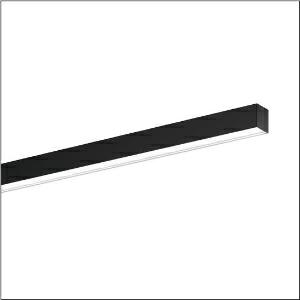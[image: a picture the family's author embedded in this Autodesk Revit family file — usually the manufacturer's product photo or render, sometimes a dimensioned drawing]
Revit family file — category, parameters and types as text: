
# Revit family: silica_r__21_51mx20tat2b_5805
name_source: partatom
category: Lighting Fixtures
units: mm (PartAtom-declared; Revit-internal decimal feet)

## family parameters
Cut with Voids When Loaded = No
Host = Face
Light Source = No
Part Type = Normal
Room Calculation Point = No
Round Connector Dimension = Use Diameter
Shared = No

## types (1)
- --- (1 x LED, 2400 lm, 20.5 W, 6500K)
    Apparent Load = 21 VA
    CIE Flux Codes = 48 79 96 100 100
    Color Rendering = 80
    Color Temperature = 6500K
    Default Elevation = 1800 mm
    Description = Silica® 21, office luminaire, primary optical cover: cover, of PMMA, opal, light emission: direct distribution, primary light characteristic: symmetric, installation type: surface-mounted, LED, rated luminous flux: 2.400lm, luminous efficacy: 112lm/W, light colour: 8tw, colour temperature: 2700..6500K, control gear: ECG DALI, with terminal, 3+2-pole, max. 2.5mm², mains connection: 220..240V, AC, 50/60Hz, rated input power: 21.5W, luminaire housing, of aluminium, jet black (RAL 9005), length: 1.204mm, width: 53mm, height: 53mm, protection rating (complete): IP20, insulation class (complete): insulation class I (protective earthing), certification: CE, permissible operating ambient temperature: 0..+35°C, standard: EN 50419, packaging unit: 1 piece
    Height = 0 mm  [stored 0 ft]
    Lamp = 1 x LED
    Lamp Light Flux = 2400 lm
    Lamp Power = 20.5 W
    Lamp count = 1
    Length = 1204 mm
    Luminous efficacy = 117 lm/W
    Manufacturer = Siteco
    ModVariant = No
    Model = 51MX20TAT2B
    Mounting Place = Ceiling
    Mounting Type = Recessed
    Number of Poles = 1
    OnlyDefault = Yes
    Power Factor = 1
    Product Name = Silica® 21
    Product group = office luminaire | ceiling recessed
    ProductGroupID = 401
    Protection Class = Protection class I
    Protection Degree = IP 20
    RLX_Detail_Level = 1
    RLX_Emergency_Light_Flux = 0 lm
    RLX_Emergency_Type = 0
    RLX_Emergency_Type_DB = No
    RlxData = <blob elided: 25629 chars, md5=88ea9f4e>
    Socket = socket
    Standby Power = 0 W
    System Light Flux = 2400 lm
    System Power = 21 W
    Type Comments = individual setting
    Type Image = l_1313584.jpg
    URL = http://relux.com
    VarID = @adj_089061
    Voltage = 0 V
    Weight = 0.00 kg
    Width = 53 mm

note: [stored X ft] marks values corroborated as IEEE doubles in the binary element streams (Revit-internal decimal feet)

## geometry (parser evidence)
native form markers: Blend x4, Sweep x10
no freeform markers — native parametric forms only
